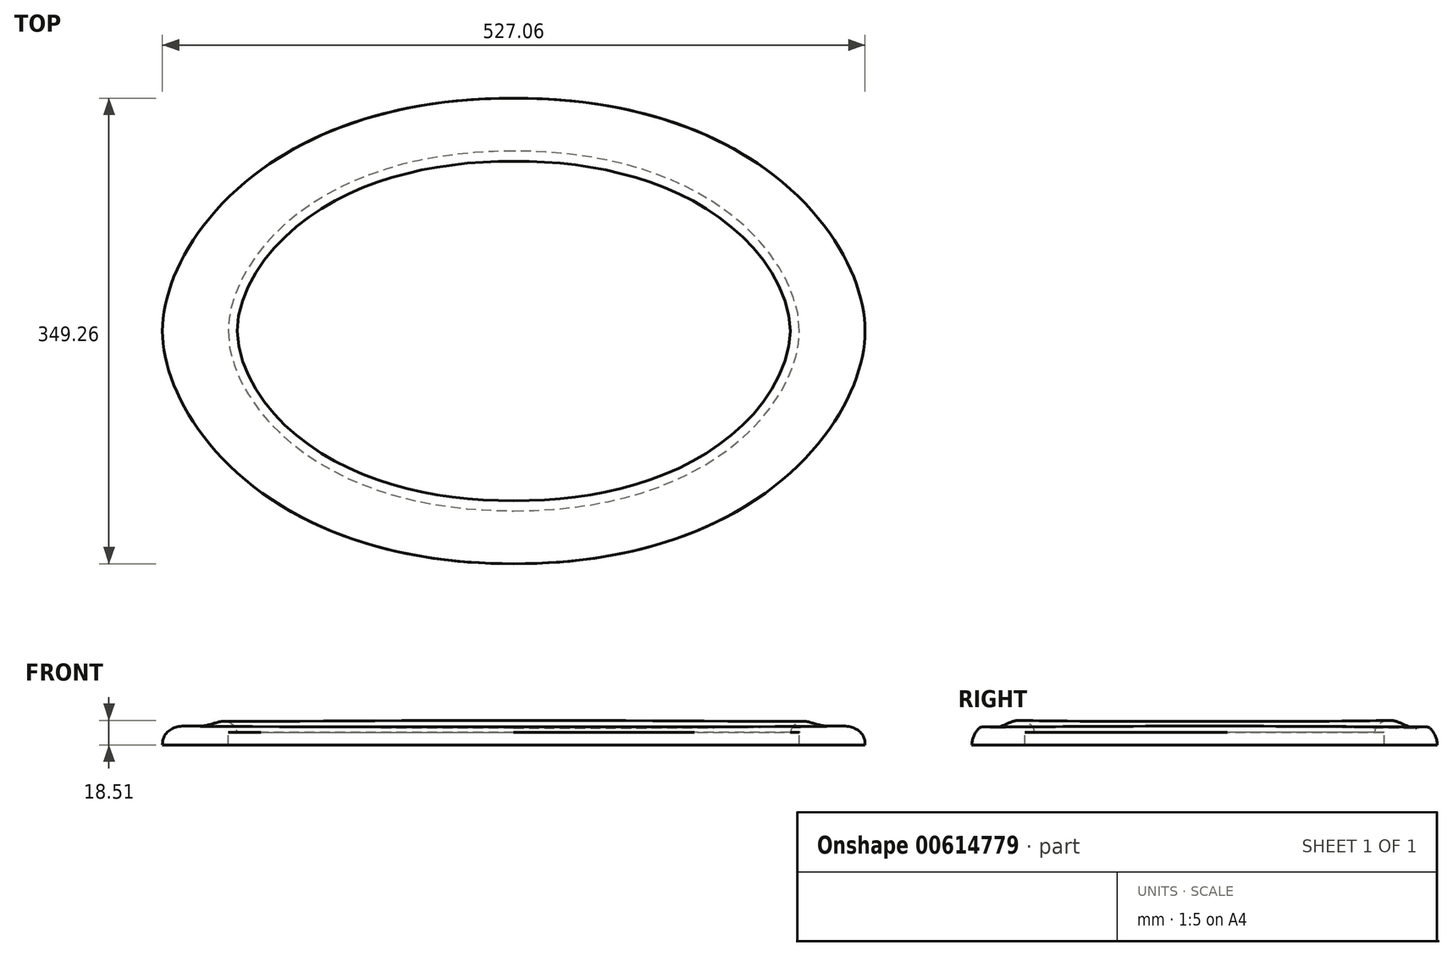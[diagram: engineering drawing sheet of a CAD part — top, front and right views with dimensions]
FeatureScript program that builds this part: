
annotation { "Feature Type Name" : "Feature", "Feature Type Description" : "" }
export const myFeature = defineFeature(function(context is Context, id is Id, definition is map)
    precondition{}
    {
        {
            var Q0;
            Q0=qCreatedBy(makeId("Top.planeOp"),FACE);
            var sketch = newSketch(context, id + "F0", { "sketchPlane" : qUnion([Q0])});
            skEllipticalArc(sketch, "E0", {});
            skEllipticalArc(sketch, "E1", {"construction": true});
            skEllipticalArc(sketch, "E2", {});
            skEllipticalArc(sketch, "E3", {"construction": true});
            const initialGuessF0  = {"E0": [0, 0, 1, 0, 0.206375, 0.127, 3.141592653589793, 4.71238898038469], "E1": [0, 0, 1, 0, 0.206375, 0.127, 4.71238898038469, 0], "E2": [0, 0, 1, 0, 0.206375, 0.127, 0, 1.5707963267948966], "E3": [0, 0, 1, 0, 0.206375, 0.127, 1.5707963267948966, 3.141592653589793]};
            skSetInitialGuess(sketch, initialGuessF0);
            skSolve(sketch);
        }
        {
            var Q0;
            Q0=qCreatedBy(makeId("Front.planeOp"),FACE);
            var sketch = newSketch(context, id + "F1", { "sketchPlane" : qUnion([Q0])});
            skLineSegment(sketch, "E4", {"start": v(-206.38, 0) * mm, "end": v(-263.53, 0) * mm});
            skFitSpline(sketch, "E5", {"points": [v(-263.53, 0) * mm, v(-252.38, 13.67) * mm, v(-231.73, 14.59) * mm, v(-215.57, 17.78) * mm, v(-206.38, 0) * mm], "startDerivative": vector(0.32, 101.91) * mm, "endDerivative": vector(-3.6, -133.31) * mm});
            skSolve(sketch);
        }
        {
            var Q0;
            Q0=qCreatedBy(makeId("Right.planeOp"),FACE);
            var sketch = newSketch(context, id + "F2", { "sketchPlane" : qUnion([Q0])});
            skLineSegment(sketch, "E6", {"start": v(-127, 0) * mm, "end": v(-174.62, 0) * mm});
            skFitSpline(sketch, "E7", {"points": [v(-127, 0) * mm, v(-128.45, 12.7) * mm, v(-140.62, 18.41) * mm, v(-158.1, 12.7) * mm, v(-167.96, 13.33) * mm, v(-174.62, 0) * mm], "startDerivative": vector(-1.26, 52.43) * mm, "endDerivative": vector(0.23, -68.62) * mm});
            skSolve(sketch);
        }
        {
            var Q0;
            Q0 = qSketchRegion(id + "F1", true);
            var Q1;
            Q1 = qSketchRegion(id + "F2", true);
            var Q2;
            Q2=sQuery(id+"F0.wireOp",EDGE,"E0");
            loft(context, id + "F3", {"startCondition" : LoftEndDerivativeType.NORMAL_TO_PROFILE, "startMagnitude" : 1, "endCondition" : LoftEndDerivativeType.NORMAL_TO_PROFILE, "endMagnitude" : 2.1, "sheetProfilesArray" : [{ "sheetProfileEntities" : qUnion([Q0]) }, { "sheetProfileEntities" : qUnion([Q1]) }], "guidesArray" : [{ "guideEntities" : qUnion([Q2]), "guideDerivativeType" : LoftGuideDerivativeType.DEFAULT, "guideDerivativeMagnitude" : 1 }]});
        }
        {
            var Q0;
            Q0=makeQuery(id+"F3.opLoft","SWEPT_BODY",BODY,{"disambiguationData":[OSD([makeQuery(id+"F1.imprint","IMPRINT",FACE,{"disambiguationData":[TD([[makeQuery(id+"F1.imprint","IMPRINT",EDGE,{"derivedFrom":sQuery(id+"F1.wireOp",EDGE,"E4")}),-1.0]])]}),makeQuery(id+"F2.imprint","IMPRINT",FACE,{"disambiguationData":[TD([[makeQuery(id+"F2.imprint","IMPRINT",EDGE,{"derivedFrom":sQuery(id+"F2.wireOp",EDGE,"E6")}),-1.0]])]})])]});
            var Q1;
            Q1=qCreatedBy(makeId("Front.planeOp"),FACE);
            mirror(context, id + "F4", {"operationType" : NewBodyOperationType.ADD, "entities" : qUnion([Q0]), "mirrorPlane" : qUnion([Q1])});
        }
        {
            var Q0;
            Q0=makeQuery(id+"F3.opLoft","SWEPT_BODY",BODY,{"disambiguationData":[OSD([makeQuery(id+"F1.imprint","IMPRINT",FACE,{"disambiguationData":[TD([[makeQuery(id+"F1.imprint","IMPRINT",EDGE,{"derivedFrom":sQuery(id+"F1.wireOp",EDGE,"E4")}),-1.0]])]}),makeQuery(id+"F2.imprint","IMPRINT",FACE,{"disambiguationData":[TD([[makeQuery(id+"F2.imprint","IMPRINT",EDGE,{"derivedFrom":sQuery(id+"F2.wireOp",EDGE,"E6")}),-1.0]])]})])]});
            var Q1;
            Q1=qCreatedBy(makeId("Right.planeOp"),FACE);
            mirror(context, id + "F5", {"operationType" : NewBodyOperationType.ADD, "entities" : qUnion([Q0]), "mirrorPlane" : qUnion([Q1])});
        }
        {
            var Q0;
            Q0=qCreatedBy(makeId("Right.planeOp"),FACE);
            var sketch = newSketch(context, id + "F6", { "sketchPlane" : qUnion([Q0])});
            skLineSegment(sketch, "E8.bottom", {"start": v(-134.92, 0) * mm, "end": v(-124.76, 0) * mm});
            skLineSegment(sketch, "E8.top", {"start": v(-134.92, 9.53) * mm, "end": v(-124.76, 9.53) * mm});
            skLineSegment(sketch, "E8.left", {"start": v(-134.92, 0) * mm, "end": v(-134.92, 9.53) * mm});
            skLineSegment(sketch, "E8.right", {"start": v(-124.76, 0) * mm, "end": v(-124.76, 9.53) * mm});
            skSolve(sketch);
        }
        {
            var Q0;
            Q0 = qSketchRegion(id + "F6", true);
            var Q1;
            {var subQ0=sQuery(id+"F2.wireOp",EDGE,"E7");var subQ1=sQuery(id+"F2.wireOp",EDGE,"E6");var subQ2=sQuery(id+"F1.wireOp",EDGE,"E5");var subQ3=sQuery(id+"F1.wireOp",EDGE,"E4");Q1=makeQuery(id+"F5.opPattern","COPY",EDGE,{"derivedFrom":makeQuery(id+"F3.opLoft","SWEPT_EDGE",EDGE,{"disambiguationData":[OSD([subQ3,subQ2,subQ1,subQ0]),TDD([makeQuery(id+"F1.imprint","INTERSECT",VERTEX,{"disambiguationData":[OD(0.0)],"derivedFrom":[subQ3,subQ2]}),makeQuery(id+"F2.imprint","INTERSECT",VERTEX,{"disambiguationData":[OD(0.0)],"derivedFrom":[subQ1,subQ0]})])]}),"instanceName":"1"});}
            var Q2;
            {var subQ0=sQuery(id+"F2.wireOp",EDGE,"E7");var subQ1=sQuery(id+"F2.wireOp",EDGE,"E6");var subQ2=sQuery(id+"F1.wireOp",EDGE,"E5");var subQ3=sQuery(id+"F1.wireOp",EDGE,"E4");Q2=makeQuery(id+"F3.opLoft","SWEPT_EDGE",EDGE,{"disambiguationData":[OSD([subQ3,subQ2,subQ1,subQ0]),TDD([makeQuery(id+"F1.imprint","INTERSECT",VERTEX,{"disambiguationData":[OD(0.0)],"derivedFrom":[subQ3,subQ2]}),makeQuery(id+"F2.imprint","INTERSECT",VERTEX,{"disambiguationData":[OD(0.0)],"derivedFrom":[subQ1,subQ0]})])]});}
            var Q3;
            {var subQ0=sQuery(id+"F2.wireOp",EDGE,"E7");var subQ1=sQuery(id+"F2.wireOp",EDGE,"E6");var subQ2=sQuery(id+"F1.wireOp",EDGE,"E5");var subQ3=sQuery(id+"F1.wireOp",EDGE,"E4");Q3=makeQuery(id+"F4.opPattern","COPY",EDGE,{"derivedFrom":makeQuery(id+"F3.opLoft","SWEPT_EDGE",EDGE,{"disambiguationData":[OSD([subQ3,subQ2,subQ1,subQ0]),TDD([makeQuery(id+"F1.imprint","INTERSECT",VERTEX,{"disambiguationData":[OD(0.0)],"derivedFrom":[subQ3,subQ2]}),makeQuery(id+"F2.imprint","INTERSECT",VERTEX,{"disambiguationData":[OD(0.0)],"derivedFrom":[subQ1,subQ0]})])]}),"instanceName":"1"});}
            var Q4;
            {var subQ0=sQuery(id+"F2.wireOp",EDGE,"E7");var subQ1=sQuery(id+"F2.wireOp",EDGE,"E6");var subQ2=sQuery(id+"F1.wireOp",EDGE,"E5");var subQ3=sQuery(id+"F1.wireOp",EDGE,"E4");Q4=makeQuery(id+"F5.opPattern","COPY",EDGE,{"derivedFrom":makeQuery(id+"F4.opPattern","COPY",EDGE,{"derivedFrom":makeQuery(id+"F3.opLoft","SWEPT_EDGE",EDGE,{"disambiguationData":[OSD([subQ3,subQ2,subQ1,subQ0]),TDD([makeQuery(id+"F1.imprint","INTERSECT",VERTEX,{"disambiguationData":[OD(0.0)],"derivedFrom":[subQ3,subQ2]}),makeQuery(id+"F2.imprint","INTERSECT",VERTEX,{"disambiguationData":[OD(0.0)],"derivedFrom":[subQ1,subQ0]})])]}),"instanceName":"1"}),"instanceName":"1"});}
            sweep(context, id + "F7", {"operationType" : NewBodyOperationType.REMOVE, "profiles" : qUnion([Q0]), "path" : qUnion([Q1, Q2, Q3, Q4])});
        }
    });
